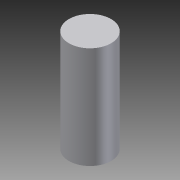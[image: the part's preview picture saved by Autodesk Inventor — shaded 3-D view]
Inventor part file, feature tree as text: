
AUTODESK INVENTOR PART (.ipt)
format: ipt  version: 2012 (Build 160160000, 160)  size: 80,384 bytes
history: native  units: mm
features: extrude x1, sketch x1
ambient origin geometry x8: Origin, YZ Plane, XZ Plane, XY Plane, X Axis, Y Axis, Z Axis, Center Point
bodies: Solid1 (feature_tree)
feature tree (2):
  extrude  "Extrusion1"  TaperAngle=0.0deg  [1 undecoded]
  sketch  "Sketch1"  dims[d2=0.0mm d3=0.0mm d4=0.0mm d9=0.0mm d10=0.0mm]
note: 1 required parameter value undecoded (feature->parameter linkage not recoverable at this tier; creation-order binding heuristic only, values carry confidence <= 0.55)
